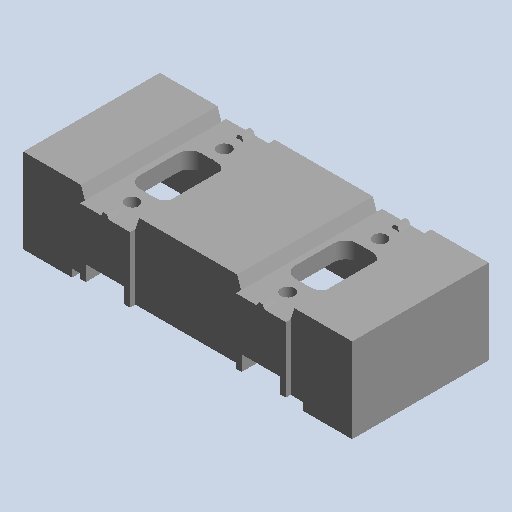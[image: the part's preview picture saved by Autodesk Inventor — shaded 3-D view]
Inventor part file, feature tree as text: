
AUTODESK INVENTOR PART (.ipt)
format: ipt  version: 2022.1 (Build 261234000, 234)  size: 175,104 bytes
history: native  units: mm (DEFAULTED — no unit token found)
features: other x8, chamfer x1
bodies: Body1 (feature_tree)
feature tree (9):
  other  "Sólido1"
  other  "Origen"
  other  "Plano YZ"
  other  "Plano XZ"
  other  "Plano XY"
  other  "Eje X"
  other  "Eje Y"
  other  "Eje Z"
  chamfer  "Chamfer1"  [1 undecoded]
note: 1 required parameter value undecoded (feature->parameter linkage not recoverable at this tier; creation-order binding heuristic only, values carry confidence <= 0.55)
